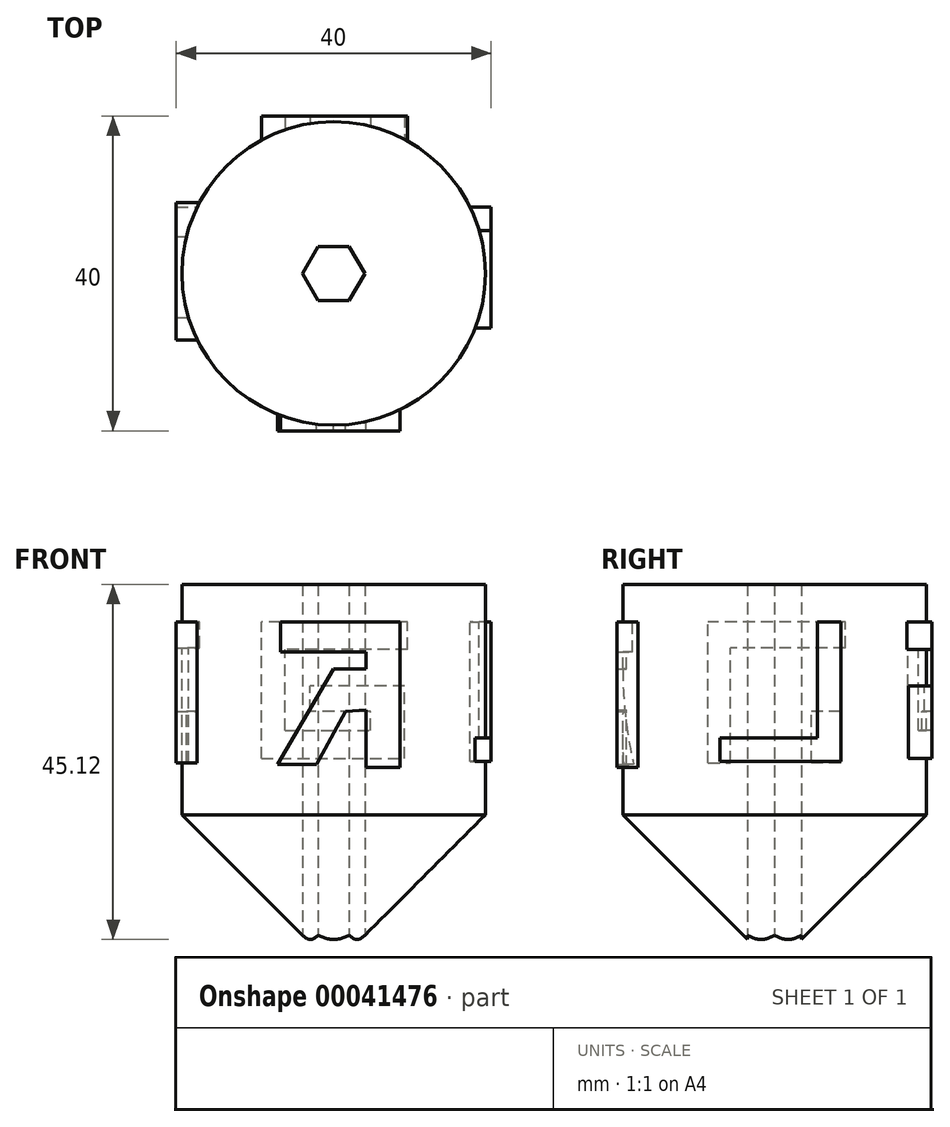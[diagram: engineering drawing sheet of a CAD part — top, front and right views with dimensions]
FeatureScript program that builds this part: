
annotation { "Feature Type Name" : "Feature", "Feature Type Description" : "" }
export const myFeature = defineFeature(function(context is Context, id is Id, definition is map)
    precondition{}
    {
        {
            var Q0;
            Q0=qCreatedBy(makeId("Front.planeOp"),FACE);
            var sketch = newSketch(context, id + "F0", { "sketchPlane" : qUnion([Q0])});
            skLineSegment(sketch, "E0.bottom", {"start": v(0, 4.77) * mm, "end": v(-19.27, 4.77) * mm});
            skLineSegment(sketch, "E0.top", {"start": v(0, -24.5) * mm, "end": v(-19.27, -24.5) * mm});
            skLineSegment(sketch, "E0.left", {"start": v(0, 4.77) * mm, "end": v(0, -24.5) * mm});
            skLineSegment(sketch, "E0.right", {"start": v(-19.27, 4.77) * mm, "end": v(-19.27, -24.5) * mm});
            skLineSegment(sketch, "E1", {"start": v(-19.27, -24.5) * mm, "end": v(0, -43.78) * mm});
            skLineSegment(sketch, "E2", {"start": v(0, -43.78) * mm, "end": v(0, -24.5) * mm});
            skLineSegment(sketch, "E3.bottom", {"start": v(0, 4.77) * mm, "end": v(-4.55, 4.77) * mm});
            skSolve(sketch);
        }
        {
            var Q0;
            Q0 = qSketchRegion(id + "F0", true);
            var Q1;
            Q1=sQuery(id+"F0.wireOp",EDGE,"E0.left");
            revolve(context, id + "F1", {"entities" : qUnion([Q0]), "axis" : qUnion([Q1]), "revolveType" : RevolveType.FULL});
        }
        {
            var Q0;
            Q0=qCreatedBy(makeId("Top.planeOp"),FACE);
            var sketch = newSketch(context, id + "F2", { "sketchPlane" : qUnion([Q0])});
            skCircle(sketch, "E4.cCircle", {"center": v(0, 0) * mm, "radius": 3.43 * mm, "construction": true});
            skLineSegment(sketch, "E4.0", {"start": v(1.98, -3.43) * mm, "end": v(-1.98, -3.43) * mm});
            skLineSegment(sketch, "E4.1", {"start": v(-1.98, -3.43) * mm, "end": v(-3.96, 0) * mm});
            skLineSegment(sketch, "E4.2", {"start": v(-3.96, 0) * mm, "end": v(-1.98, 3.43) * mm});
            skLineSegment(sketch, "E4.3", {"start": v(-1.98, 3.43) * mm, "end": v(1.98, 3.43) * mm});
            skLineSegment(sketch, "E4.4", {"start": v(1.98, 3.43) * mm, "end": v(3.96, 0) * mm});
            skLineSegment(sketch, "E4.5", {"start": v(3.96, 0) * mm, "end": v(1.98, -3.43) * mm});
            skPoint(sketch, "E4.0.midPoint", {"position": v(0, -3.43) * mm});
            skSolve(sketch);
        }
        {
            var Q0;
            Q0=qCreatedBy(makeId("Right.planeOp"),FACE);
            var sketch = newSketch(context, id + "F3", { "sketchPlane" : qUnion([Q0])});
            skLineSegment(sketch, "E5.bottom", {"start": v(8.44, 0) * mm, "end": v(5.44, 0) * mm});
            skLineSegment(sketch, "E5.top", {"start": v(8.44, -14.73) * mm, "end": v(5.44, -14.73) * mm});
            skLineSegment(sketch, "E5.left", {"start": v(8.44, 0) * mm, "end": v(8.44, -14.73) * mm});
            skLineSegment(sketch, "E5.right", {"start": v(5.44, 0) * mm, "end": v(5.44, -14.73) * mm});
            skLineSegment(sketch, "E6.bottom", {"start": v(8.44, -14.73) * mm, "end": v(-6.94, -14.73) * mm});
            skLineSegment(sketch, "E6.top", {"start": v(8.44, -17.73) * mm, "end": v(-6.94, -17.73) * mm});
            skLineSegment(sketch, "E6.left", {"start": v(8.44, -14.73) * mm, "end": v(8.44, -17.73) * mm});
            skLineSegment(sketch, "E6.right", {"start": v(-6.94, -14.73) * mm, "end": v(-6.94, -17.73) * mm});
            skSolve(sketch);
        }
        {
            var Q0;
            Q0 = qSketchRegion(id + "F2", true);
            extrude(context, id + "F4", {"entities" : qUnion([Q0]), "operationType" : NewBodyOperationType.REMOVE, "depth" : 71.64 * mm});
        }
        {
            var Q0;
            Q0 = qSketchRegion(id + "F3", true);
            extrude(context, id + "F5", {"entities" : qUnion([Q0]), "operationType" : NewBodyOperationType.ADD, "depth" : 20 * mm});
        }
        {
            var Q0;
            Q0=qCreatedBy(makeId("Right.planeOp"),FACE);
            var sketch = newSketch(context, id + "F6", { "sketchPlane" : qUnion([Q0])});
            skLineSegment(sketch, "E7.bottom", {"start": v(9, 0) * mm, "end": v(-8.44, 0) * mm});
            skLineSegment(sketch, "E7.top", {"start": v(9, -3.28) * mm, "end": v(-8.44, -3.28) * mm});
            skLineSegment(sketch, "E7.left", {"start": v(9, 0) * mm, "end": v(9, -3.28) * mm});
            skLineSegment(sketch, "E7.right", {"start": v(-8.44, 0) * mm, "end": v(-8.44, -3.28) * mm});
            skLineSegment(sketch, "E8.bottom", {"start": v(-8.44, -3.28) * mm, "end": v(-5.63, -3.28) * mm});
            skLineSegment(sketch, "E8.top", {"start": v(-8.44, -17.92) * mm, "end": v(-5.63, -17.92) * mm});
            skLineSegment(sketch, "E8.left", {"start": v(-8.44, -3.28) * mm, "end": v(-8.44, -17.92) * mm});
            skLineSegment(sketch, "E8.right", {"start": v(-5.63, -3.28) * mm, "end": v(-5.63, -17.92) * mm});
            skLineSegment(sketch, "E9.bottom", {"start": v(8.44, -17.92) * mm, "end": v(4.69, -17.92) * mm});
            skLineSegment(sketch, "E9.top", {"start": v(8.44, -11.35) * mm, "end": v(4.69, -11.35) * mm});
            skLineSegment(sketch, "E9.left", {"start": v(8.44, -17.92) * mm, "end": v(8.44, -11.35) * mm});
            skLineSegment(sketch, "E9.right", {"start": v(4.69, -17.92) * mm, "end": v(4.69, -11.35) * mm});
            skSolve(sketch);
        }
        {
            var Q0;
            Q0 = qSketchRegion(id + "F6", true);
            extrude(context, id + "F7", {"entities" : qUnion([Q0]), "operationType" : NewBodyOperationType.ADD, "oppositeDirection" : true, "depth" : 20 * mm});
        }
        {
            var Q0;
            Q0=qCreatedBy(makeId("Front.planeOp"),FACE);
            var sketch = newSketch(context, id + "F8", { "sketchPlane" : qUnion([Q0])});
            skLineSegment(sketch, "E10.bottom", {"start": v(-6.75, 0) * mm, "end": v(8.44, 0) * mm});
            skLineSegment(sketch, "E10.top", {"start": v(-6.75, -3.85) * mm, "end": v(8.44, -3.85) * mm});
            skLineSegment(sketch, "E10.left", {"start": v(-6.75, 0) * mm, "end": v(-6.75, -3.85) * mm});
            skLineSegment(sketch, "E10.right", {"start": v(8.44, 0) * mm, "end": v(8.44, -3.85) * mm});
            skLineSegment(sketch, "E11.bottom", {"start": v(8.44, -3.85) * mm, "end": v(4.13, -3.85) * mm});
            skLineSegment(sketch, "E11.top", {"start": v(8.44, -18.48) * mm, "end": v(4.13, -18.48) * mm});
            skLineSegment(sketch, "E11.left", {"start": v(8.44, -3.85) * mm, "end": v(8.44, -18.48) * mm});
            skLineSegment(sketch, "E11.right", {"start": v(4.13, -3.85) * mm, "end": v(4.13, -18.48) * mm});
            skLineSegment(sketch, "E12", {"start": v(4.13, -6) * mm, "end": v(0, -6) * mm});
            skLineSegment(sketch, "E13", {"start": v(0, -6) * mm, "end": v(-7.13, -18.1) * mm});
            skLineSegment(sketch, "E14", {"start": v(-7.13, -18.1) * mm, "end": v(-2.2, -18.1) * mm});
            skLineSegment(sketch, "E15", {"start": v(-2.2, -18.1) * mm, "end": v(1.5, -11.35) * mm});
            skLineSegment(sketch, "E16", {"start": v(1.5, -11.35) * mm, "end": v(4.13, -11.16) * mm});
            skLineSegment(sketch, "E17", {"start": v(4.13, -11.16) * mm, "end": v(4.31, -7.79) * mm});
            skSolve(sketch);
        }
        {
            var Q0;
            Q0 = qSketchRegion(id + "F8", true);
            extrude(context, id + "F9", {"entities" : qUnion([Q0]), "operationType" : NewBodyOperationType.ADD, "depth" : 20 * mm});
        }
        {
            var Q0;
            Q0=qCreatedBy(makeId("Front.planeOp"),FACE);
            var sketch = newSketch(context, id + "F10", { "sketchPlane" : qUnion([Q0])});
            skLineSegment(sketch, "E18.bottom", {"start": v(9.38, 0) * mm, "end": v(-9.2, 0) * mm});
            skLineSegment(sketch, "E18.top", {"start": v(9.38, -3.47) * mm, "end": v(-9.2, -3.47) * mm});
            skLineSegment(sketch, "E18.left", {"start": v(9.38, 0) * mm, "end": v(9.38, -3.47) * mm});
            skLineSegment(sketch, "E18.right", {"start": v(-9.2, 0) * mm, "end": v(-9.2, -3.47) * mm});
            skLineSegment(sketch, "E19.bottom", {"start": v(-9.2, -3.47) * mm, "end": v(-6.2, -3.47) * mm});
            skLineSegment(sketch, "E19.top", {"start": v(-9.2, -17.35) * mm, "end": v(-6.2, -17.35) * mm});
            skLineSegment(sketch, "E19.left", {"start": v(-9.2, -3.47) * mm, "end": v(-9.2, -17.35) * mm});
            skLineSegment(sketch, "E19.right", {"start": v(-6.2, -3.47) * mm, "end": v(-6.2, -17.35) * mm});
            skLineSegment(sketch, "E20.bottom", {"start": v(-6.2, -17.35) * mm, "end": v(9, -17.35) * mm});
            skLineSegment(sketch, "E20.top", {"start": v(-6.2, -13.79) * mm, "end": v(9, -13.79) * mm});
            skLineSegment(sketch, "E20.left", {"start": v(-6.2, -17.35) * mm, "end": v(-6.2, -13.79) * mm});
            skLineSegment(sketch, "E20.right", {"start": v(9, -17.35) * mm, "end": v(9, -13.79) * mm});
            skLineSegment(sketch, "E21.bottom", {"start": v(9, -13.79) * mm, "end": v(4.69, -13.79) * mm});
            skLineSegment(sketch, "E22.top", {"start": v(9, -8.16) * mm, "end": v(4.69, -8.16) * mm});
            skLineSegment(sketch, "E22.left", {"start": v(9, -13.79) * mm, "end": v(9, -8.16) * mm});
            skLineSegment(sketch, "E22.right", {"start": v(4.69, -13.79) * mm, "end": v(4.69, -8.16) * mm});
            skLineSegment(sketch, "E23.bottom", {"start": v(4.69, -8.16) * mm, "end": v(-3, -8.16) * mm});
            skLineSegment(sketch, "E23.top", {"start": v(4.69, -11.35) * mm, "end": v(-3, -11.35) * mm});
            skLineSegment(sketch, "E23.left", {"start": v(4.69, -8.16) * mm, "end": v(4.69, -11.35) * mm});
            skLineSegment(sketch, "E23.right", {"start": v(-3, -8.16) * mm, "end": v(-3, -11.35) * mm});
            skSolve(sketch);
        }
        {
            var Q0;
            Q0 = qSketchRegion(id + "F10", true);
            extrude(context, id + "F11", {"entities" : qUnion([Q0]), "operationType" : NewBodyOperationType.ADD, "oppositeDirection" : true, "depth" : 20 * mm});
        }
        {
            var Q0;
            Q0=makeQuery(id+"F2.imprint","IMPRINT",FACE,{"disambiguationData":[TD([[makeQuery(id+"F2.imprint","IMPRINT",EDGE,{"derivedFrom":sQuery(id+"F2.wireOp",EDGE,"E4.0")}),-1.0]])]});
            extrude(context, id + "F12", {"entities" : qUnion([Q0]), "operationType" : NewBodyOperationType.REMOVE, "oppositeDirection" : true, "depth" : 49.92 * mm});
        }
    });
